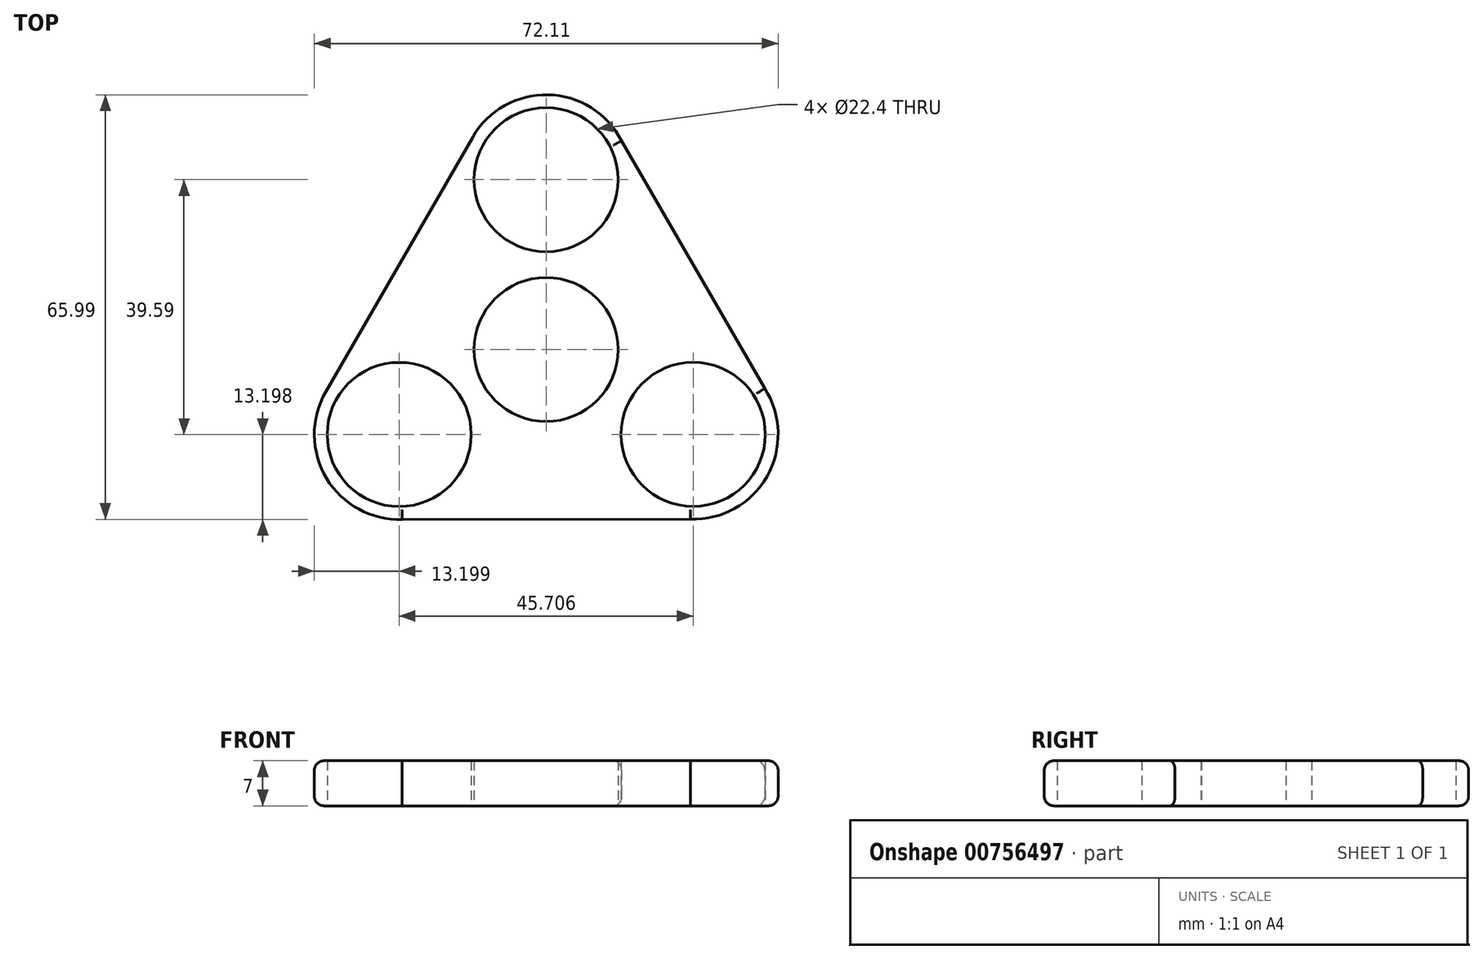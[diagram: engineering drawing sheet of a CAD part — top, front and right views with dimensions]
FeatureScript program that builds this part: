
annotation { "Feature Type Name" : "Feature", "Feature Type Description" : "" }
export const myFeature = defineFeature(function(context is Context, id is Id, definition is map)
    precondition{}
    {
        {
            var Q0;
            Q0=qCreatedBy(makeId("Top.planeOp"),FACE);
            var sketch = newSketch(context, id + "F0", { "sketchPlane" : qUnion([Q0])});
            skCircle(sketch, "E0", {"center": v(0, 0) * mm, "radius": 11.2 * mm});
            skArc(sketch, "E1.MirrorC", {"start": v(-11.43, 32.98) * mm, "mid": v(0.3, 39.59) * mm, "end": v(11.73, 32.45) * mm});
            skCircle(sketch, "E2.MirrorC", {"center": v(0, 26.39) * mm, "radius": 11.2 * mm});
            skArc(sketch, "E3.1.0", {"start": v(-22.4, -26.4) * mm, "mid": v(-34.16, -20) * mm, "end": v(-34.27, -6.6) * mm});
            skCircle(sketch, "E3.1.1", {"center": v(-22.84, -13.2) * mm, "radius": 11.2 * mm});
            skArc(sketch, "E3.2.0", {"start": v(33.97, -6.06) * mm, "mid": v(34.34, -19.7) * mm, "end": v(22.43, -26.38) * mm});
            skCircle(sketch, "E3.2.1", {"center": v(22.87, -13.19) * mm, "radius": 11.2 * mm});
            skLineSegment(sketch, "E4", {"start": v(-34.27, -6.6) * mm, "end": v(-11.43, 32.98) * mm});
            skLineSegment(sketch, "E5.1.0", {"start": v(22.43, -26.38) * mm, "end": v(-22.4, -26.4) * mm});
            skLineSegment(sketch, "E5.2.0", {"start": v(11.73, 32.45) * mm, "end": v(33.97, -6.06) * mm});
            skPoint(sketch, "E6.orphan", {"position": v(22.86, -26.38) * mm});
            skPoint(sketch, "E7.orphan", {"position": v(-22.85, -26.4) * mm});
            skPoint(sketch, "E8.orphan", {"position": v(34.28, -6.6) * mm});
            skPoint(sketch, "E9.orphan", {"position": v(11.42, 32.98) * mm});
            skSolve(sketch);
        }
        {
            var Q0;
            Q0 = qSketchRegion(id + "F0", true);
            extrude(context, id + "F1", {"entities" : qUnion([Q0]), "depth" : 7 * mm, "offsetDistance" : 25 * mm, "symmetric" : true});
        }
        {
            var Q0;
            Q0=makeQuery(id+"F1.opExtrude","CAP_EDGE",EDGE,{"disambiguationData":[OSD([sQuery(id+"F0.wireOp",EDGE,"E4")])],"isStart":false});
            var Q1;
            Q1=makeQuery(id+"F1.opExtrude","CAP_EDGE",EDGE,{"disambiguationData":[OSD([sQuery(id+"F0.wireOp",EDGE,"E1.MirrorC")])],"isStart":false});
            var Q2;
            Q2=makeQuery(id+"F1.opExtrude","CAP_EDGE",EDGE,{"disambiguationData":[OSD([sQuery(id+"F0.wireOp",EDGE,"E5.2.0")])],"isStart":false});
            var Q3;
            Q3=makeQuery(id+"F1.opExtrude","CAP_EDGE",EDGE,{"disambiguationData":[OSD([sQuery(id+"F0.wireOp",EDGE,"E3.2.0")])],"isStart":false});
            var Q4;
            Q4=makeQuery(id+"F1.opExtrude","CAP_EDGE",EDGE,{"disambiguationData":[OSD([sQuery(id+"F0.wireOp",EDGE,"E5.1.0")])],"isStart":false});
            var Q5;
            Q5=makeQuery(id+"F1.opExtrude","CAP_EDGE",EDGE,{"disambiguationData":[OSD([sQuery(id+"F0.wireOp",EDGE,"E3.1.0")])],"isStart":false});
            fillet(context, id + "F2", {"entities" : qUnion([Q0, Q1, Q2, Q3, Q4, Q5]), "radius" : 1.5 * mm, "tangentPropagation" : true, "allowEdgeOverflow" : false});
        }
        {
            var Q0;
            Q0=makeQuery(id+"F1.opExtrude","CAP_EDGE",EDGE,{"disambiguationData":[OSD([sQuery(id+"F0.wireOp",EDGE,"E5.2.0")])],"isStart":true});
            var Q1;
            Q1=makeQuery(id+"F1.opExtrude","CAP_EDGE",EDGE,{"disambiguationData":[OSD([sQuery(id+"F0.wireOp",EDGE,"E3.2.0")])],"isStart":true});
            var Q2;
            Q2=makeQuery(id+"F1.opExtrude","CAP_EDGE",EDGE,{"disambiguationData":[OSD([sQuery(id+"F0.wireOp",EDGE,"E5.1.0")])],"isStart":true});
            var Q3;
            Q3=makeQuery(id+"F1.opExtrude","CAP_EDGE",EDGE,{"disambiguationData":[OSD([sQuery(id+"F0.wireOp",EDGE,"E3.1.0")])],"isStart":true});
            var Q4;
            Q4=makeQuery(id+"F1.opExtrude","CAP_EDGE",EDGE,{"disambiguationData":[OSD([sQuery(id+"F0.wireOp",EDGE,"E4")])],"isStart":true});
            var Q5;
            Q5=makeQuery(id+"F1.opExtrude","CAP_EDGE",EDGE,{"disambiguationData":[OSD([sQuery(id+"F0.wireOp",EDGE,"E1.MirrorC")])],"isStart":true});
            fillet(context, id + "F3", {"entities" : qUnion([Q0, Q1, Q2, Q3, Q4, Q5]), "radius" : 1.5 * mm, "tangentPropagation" : true, "allowEdgeOverflow" : false});
        }
    });
